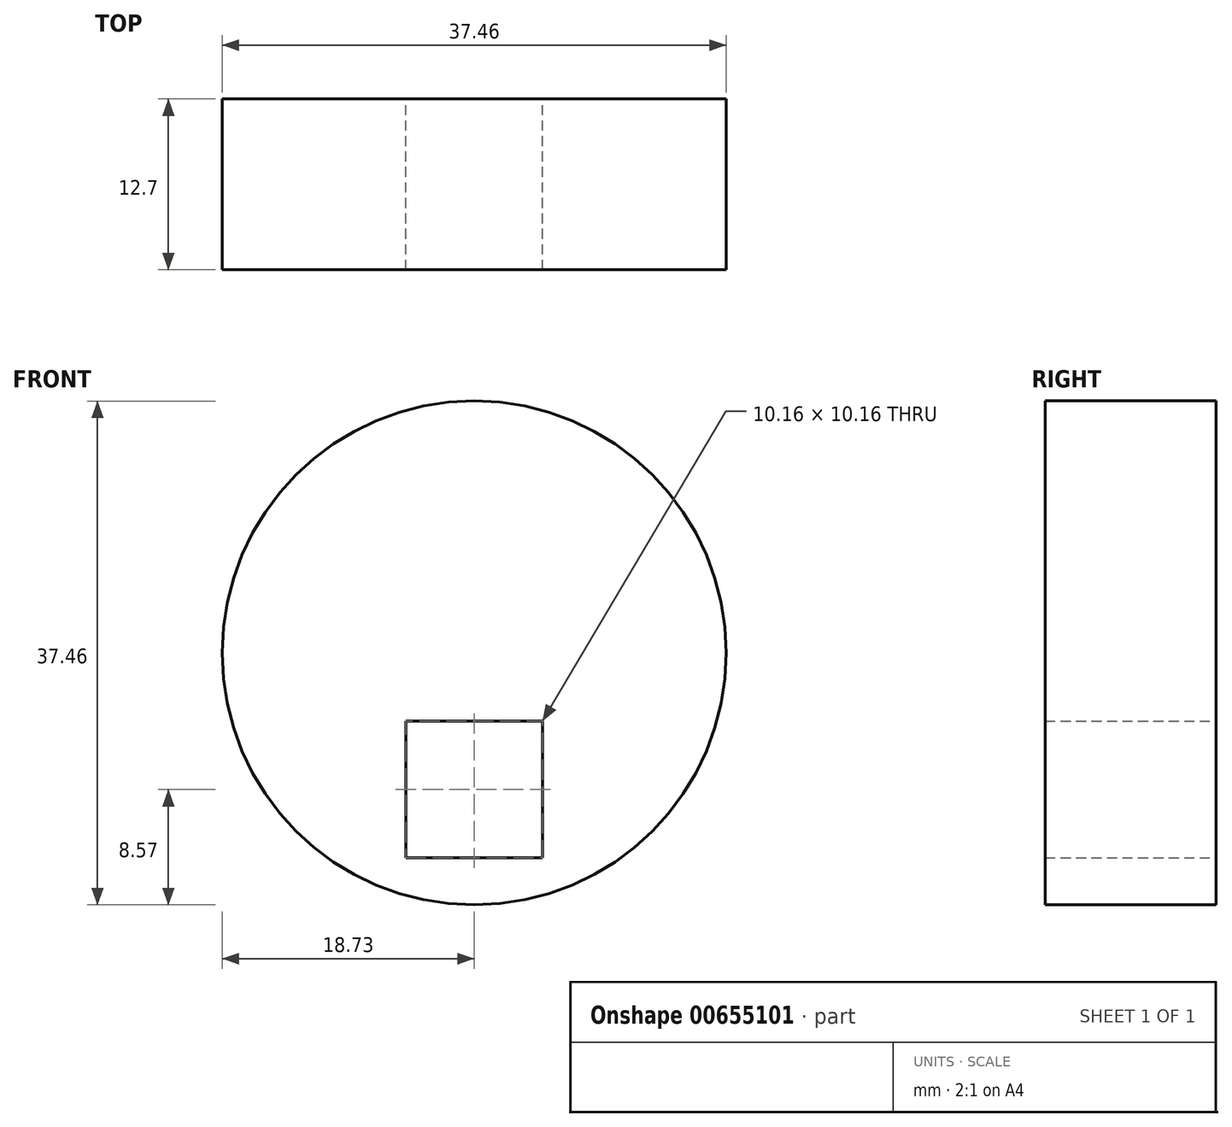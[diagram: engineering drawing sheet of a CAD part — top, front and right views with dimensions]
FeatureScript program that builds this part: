
annotation { "Feature Type Name" : "Feature", "Feature Type Description" : "" }
export const myFeature = defineFeature(function(context is Context, id is Id, definition is map)
    precondition{}
    {
        {
            var Q0;
            Q0=qCreatedBy(makeId("Front.planeOp"),FACE);
            var sketch = newSketch(context, id + "F0", { "sketchPlane" : qUnion([Q0])});
            skLineSegment(sketch, "E0.bottom", {"start": v(-5.08, 5.08) * mm, "end": v(5.08, 5.08) * mm});
            skLineSegment(sketch, "E0.top", {"start": v(-5.08, -5.08) * mm, "end": v(5.08, -5.08) * mm});
            skLineSegment(sketch, "E0.left", {"start": v(-5.08, 5.08) * mm, "end": v(-5.08, -5.08) * mm});
            skLineSegment(sketch, "E0.right", {"start": v(5.08, 5.08) * mm, "end": v(5.08, -5.08) * mm});
            skPoint(sketch, "E0.middle", {"position": v(0, 0) * mm});
            skLineSegment(sketch, "E1", {"start": v(-18.73, 10.16) * mm, "end": v(18.73, 10.16) * mm});
            skArc(sketch, "E2", {"start": v(18.73, 10.16) * mm, "mid": v(0, 28.9) * mm, "end": v(-18.73, 10.16) * mm});
            skArc(sketch, "E3", {"start": v(-18.73, 10.16) * mm, "mid": v(0, -8.57) * mm, "end": v(18.73, 10.16) * mm});
            skSolve(sketch);
        }
        {
            var Q0;
            Q0 = qSketchRegion(id + "F0", true);
            extrude(context, id + "F1", {"entities" : qUnion([Q0]), "depth" : 12.7 * mm, "offsetDistance" : 25.4 * mm});
        }
    });
